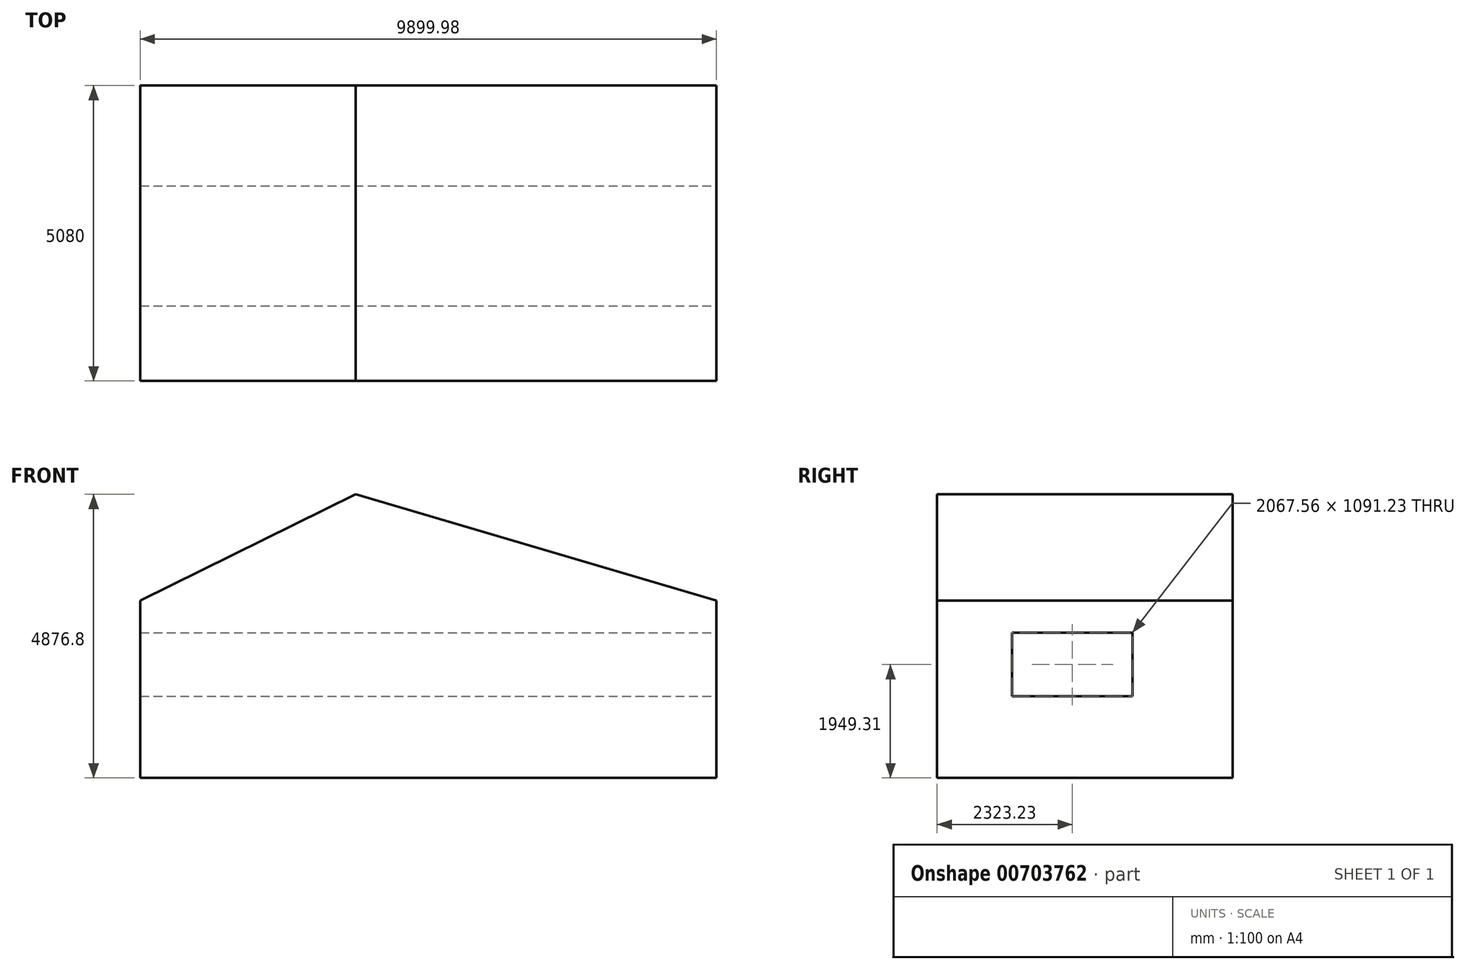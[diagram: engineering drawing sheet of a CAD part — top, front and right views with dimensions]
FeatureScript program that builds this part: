
annotation { "Feature Type Name" : "Feature", "Feature Type Description" : "" }
export const myFeature = defineFeature(function(context is Context, id is Id, definition is map)
    precondition{}
    {
        {
            var Q0;
            Q0=qCreatedBy(makeId("Front.planeOp"),FACE);
            var sketch = newSketch(context, id + "F0", { "sketchPlane" : qUnion([Q0])});
            skLineSegment(sketch, "E0", {"start": v(0, 0) * mm, "end": v(0, 3048) * mm});
            skLineSegment(sketch, "E1", {"start": v(3670.44, 0) * mm, "end": v(0, 0) * mm});
            skLineSegment(sketch, "E2", {"start": v(0, 3048) * mm, "end": v(3704.35, 4876.8) * mm});
            skLineSegment(sketch, "E3", {"start": v(3704.35, 4876.8) * mm, "end": v(9899.98, 3048) * mm});
            skLineSegment(sketch, "E4", {"start": v(9899.98, 3048) * mm, "end": v(9899.98, 0) * mm});
            skLineSegment(sketch, "E5", {"start": v(9899.98, 0) * mm, "end": v(3670.44, 0) * mm});
            skSolve(sketch);
        }
        {
            var Q0;
            Q0=makeQuery(id+"F0.imprint","IMPRINT",FACE,{"disambiguationData":[TD([[makeQuery(id+"F0.imprint","IMPRINT",EDGE,{"derivedFrom":sQuery(id+"F0.wireOp",EDGE,"E0")}),-1.0]])]});
            extrude(context, id + "F1", {"entities" : qUnion([Q0]), "depth" : 5080 * mm, "offsetDistance" : 25.4 * mm});
        }
        {
            var Q0;
            Q0=makeQuery(id+"F1.opExtrude","SWEPT_FACE",FACE,{"disambiguationData":[OSD([sQuery(id+"F0.wireOp",EDGE,"E4")])]});
            var sketch = newSketch(context, id + "F2", { "sketchPlane" : qUnion([Q0])});
            skLineSegment(sketch, "E6.bottom", {"start": v(-3790.55, 2494.93) * mm, "end": v(-1722.99, 2494.93) * mm});
            skLineSegment(sketch, "E6.top", {"start": v(-3790.55, 1403.7) * mm, "end": v(-1722.99, 1403.7) * mm});
            skLineSegment(sketch, "E6.left", {"start": v(-3790.55, 2494.93) * mm, "end": v(-3790.55, 1403.7) * mm});
            skLineSegment(sketch, "E6.right", {"start": v(-1722.99, 2494.93) * mm, "end": v(-1722.99, 1403.7) * mm});
            skSolve(sketch);
        }
        {
            var Q0;
            Q0=makeQuery(id+"F2.imprint","IMPRINT",FACE,{"disambiguationData":[TD([[makeQuery(id+"F2.imprint","IMPRINT",EDGE,{"derivedFrom":sQuery(id+"F2.wireOp",EDGE,"E6.bottom")}),-1.0]])]});
            extrude(context, id + "F3", {"entities" : qUnion([Q0]), "operationType" : NewBodyOperationType.REMOVE, "endBound" : BoundingType.THROUGH_ALL, "oppositeDirection" : true, "depth" : 25.4 * mm, "offsetDistance" : 25.4 * mm});
        }
    });
